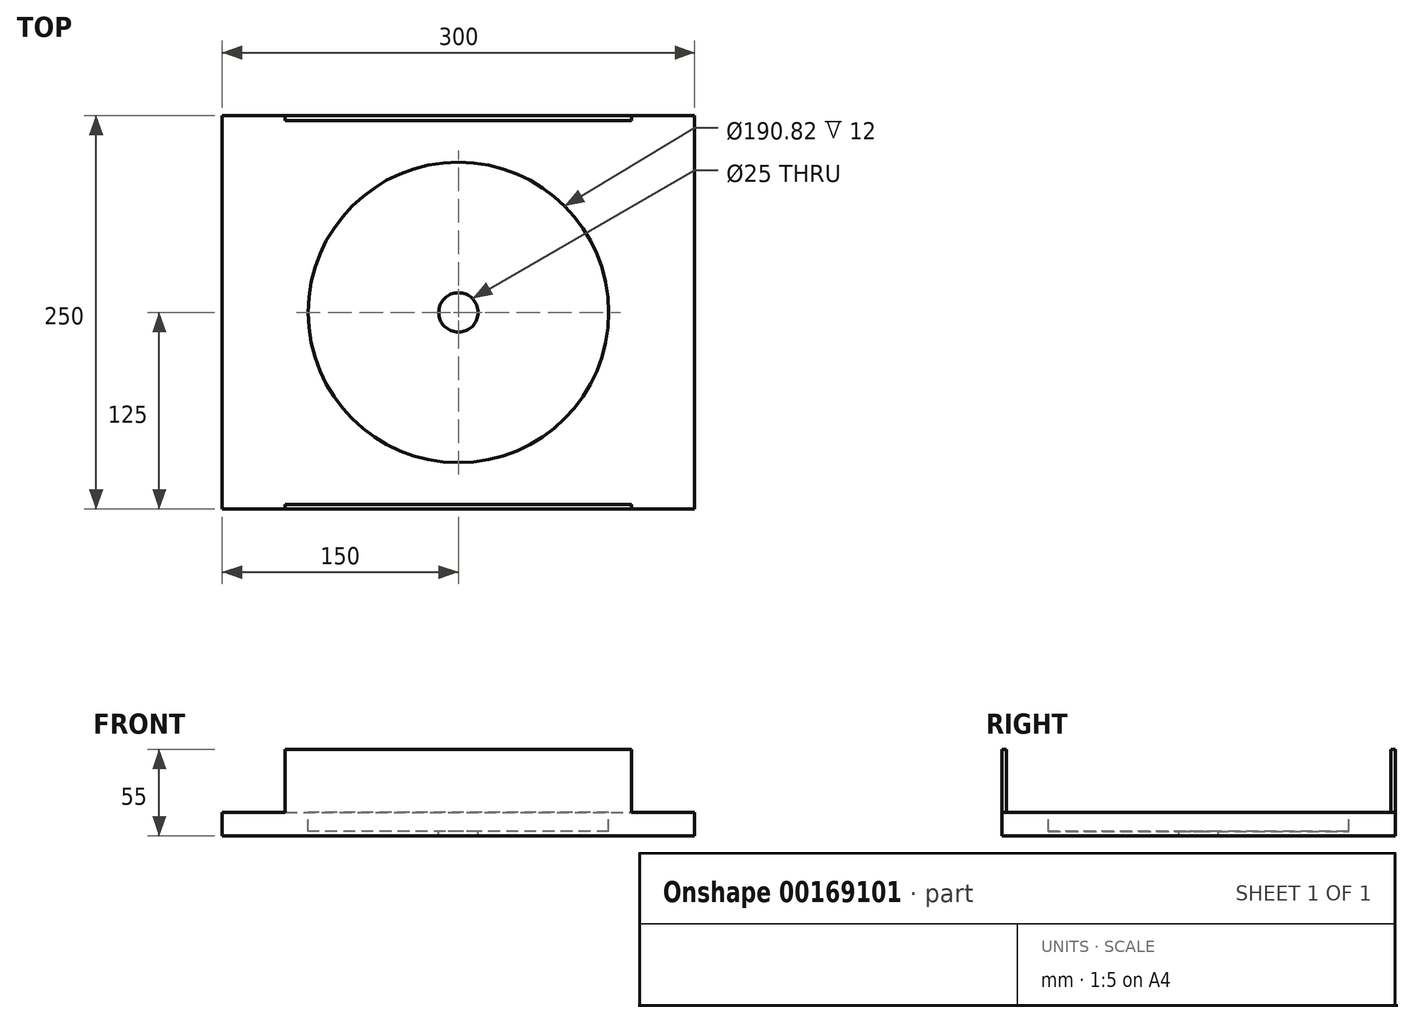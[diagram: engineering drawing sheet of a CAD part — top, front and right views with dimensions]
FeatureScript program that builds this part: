
annotation { "Feature Type Name" : "Feature", "Feature Type Description" : "" }
export const myFeature = defineFeature(function(context is Context, id is Id, definition is map)
    precondition{}
    {
        {
            var Q0;
            Q0=qCreatedBy(makeId("Top.planeOp"),FACE);
            var sketch = newSketch(context, id + "F0", { "sketchPlane" : qUnion([Q0])});
            skLineSegment(sketch, "E0.bottom", {"start": v(150, 125) * mm, "end": v(-150, 125) * mm});
            skLineSegment(sketch, "E0.top", {"start": v(150, -125) * mm, "end": v(-150, -125) * mm});
            skLineSegment(sketch, "E0.left", {"start": v(150, 125) * mm, "end": v(150, -125) * mm});
            skLineSegment(sketch, "E0.right", {"start": v(-150, 125) * mm, "end": v(-150, -125) * mm});
            skPoint(sketch, "E0.middle", {"position": v(0, 0) * mm});
            skSolve(sketch);
        }
        {
            var Q0;
            Q0 = qSketchRegion(id + "F0", true);
            extrude(context, id + "F1", {"entities" : qUnion([Q0]), "depth" : 15 * mm});
        }
        {
            var Q0;
            Q0=makeQuery(id+"F1.opExtrude","CAP_FACE",FACE,{"disambiguationData":[OSD([sQuery(id+"F0.wireOp",EDGE,"E0.bottom"),sQuery(id+"F0.wireOp",EDGE,"E0.top"),sQuery(id+"F0.wireOp",EDGE,"E0.left"),sQuery(id+"F0.wireOp",EDGE,"E0.right")])],"isStart":false});
            var sketch = newSketch(context, id + "F2", { "sketchPlane" : qUnion([Q0])});
            skCircle(sketch, "E1", {"center": v(0, 0) * mm, "radius": 95.4 * mm});
            skSolve(sketch);
        }
        {
            var Q0;
            Q0 = qSketchRegion(id + "F2", true);
            extrude(context, id + "F3", {"entities" : qUnion([Q0]), "operationType" : NewBodyOperationType.REMOVE, "oppositeDirection" : true, "depth" : 12 * mm});
        }
        {
            var Q0;
            Q0=makeQuery(id+"F1.opExtrude","CAP_FACE",FACE,{"disambiguationData":[OSD([sQuery(id+"F0.wireOp",EDGE,"E0.bottom"),sQuery(id+"F0.wireOp",EDGE,"E0.top"),sQuery(id+"F0.wireOp",EDGE,"E0.left"),sQuery(id+"F0.wireOp",EDGE,"E0.right")])],"isStart":false});
            var sketch = newSketch(context, id + "F4", { "sketchPlane" : qUnion([Q0])});
            skCircle(sketch, "E2", {"center": v(0, 0) * mm, "radius": 12.5 * mm});
            skSolve(sketch);
        }
        {
            var Q0;
            Q0 = qSketchRegion(id + "F4", true);
            extrude(context, id + "F5", {"entities" : qUnion([Q0]), "operationType" : NewBodyOperationType.REMOVE, "endBound" : BoundingType.THROUGH_ALL, "oppositeDirection" : true, "depth" : 25 * mm});
        }
        {
            var Q0;
            Q0=makeQuery(id+"F1.opExtrude","CAP_FACE",FACE,{"disambiguationData":[OSD([sQuery(id+"F0.wireOp",EDGE,"E0.bottom"),sQuery(id+"F0.wireOp",EDGE,"E0.top"),sQuery(id+"F0.wireOp",EDGE,"E0.left"),sQuery(id+"F0.wireOp",EDGE,"E0.right")])],"isStart":false});
            var sketch = newSketch(context, id + "F6", { "sketchPlane" : qUnion([Q0])});
            skLineSegment(sketch, "E3.bottom", {"start": v(-110, 125) * mm, "end": v(110, 125) * mm});
            skLineSegment(sketch, "E3.top", {"start": v(-110, 122) * mm, "end": v(110, 122) * mm});
            skLineSegment(sketch, "E3.left", {"start": v(-110, 125) * mm, "end": v(-110, 122) * mm});
            skLineSegment(sketch, "E3.right", {"start": v(110, 125) * mm, "end": v(110, 122) * mm});
            skLineSegment(sketch, "E4", {"start": v(-39.23, 0) * mm, "end": v(62.21, 0) * mm, "construction": true});
            skLineSegment(sketch, "E5.MirrorCS", {"start": v(110, -125) * mm, "end": v(110, -122) * mm});
            skLineSegment(sketch, "E6.MirrorCS", {"start": v(-110, -125) * mm, "end": v(-110, -122) * mm});
            skLineSegment(sketch, "E7.MirrorCS", {"start": v(-110, -125) * mm, "end": v(110, -125) * mm});
            skLineSegment(sketch, "E8.MirrorCS", {"start": v(-110, -122) * mm, "end": v(110, -122) * mm});
            skSolve(sketch);
        }
        {
            var Q0;
            Q0 = qSketchRegion(id + "F6", true);
            extrude(context, id + "F7", {"entities" : qUnion([Q0]), "operationType" : NewBodyOperationType.ADD, "depth" : 40 * mm});
        }
    });
